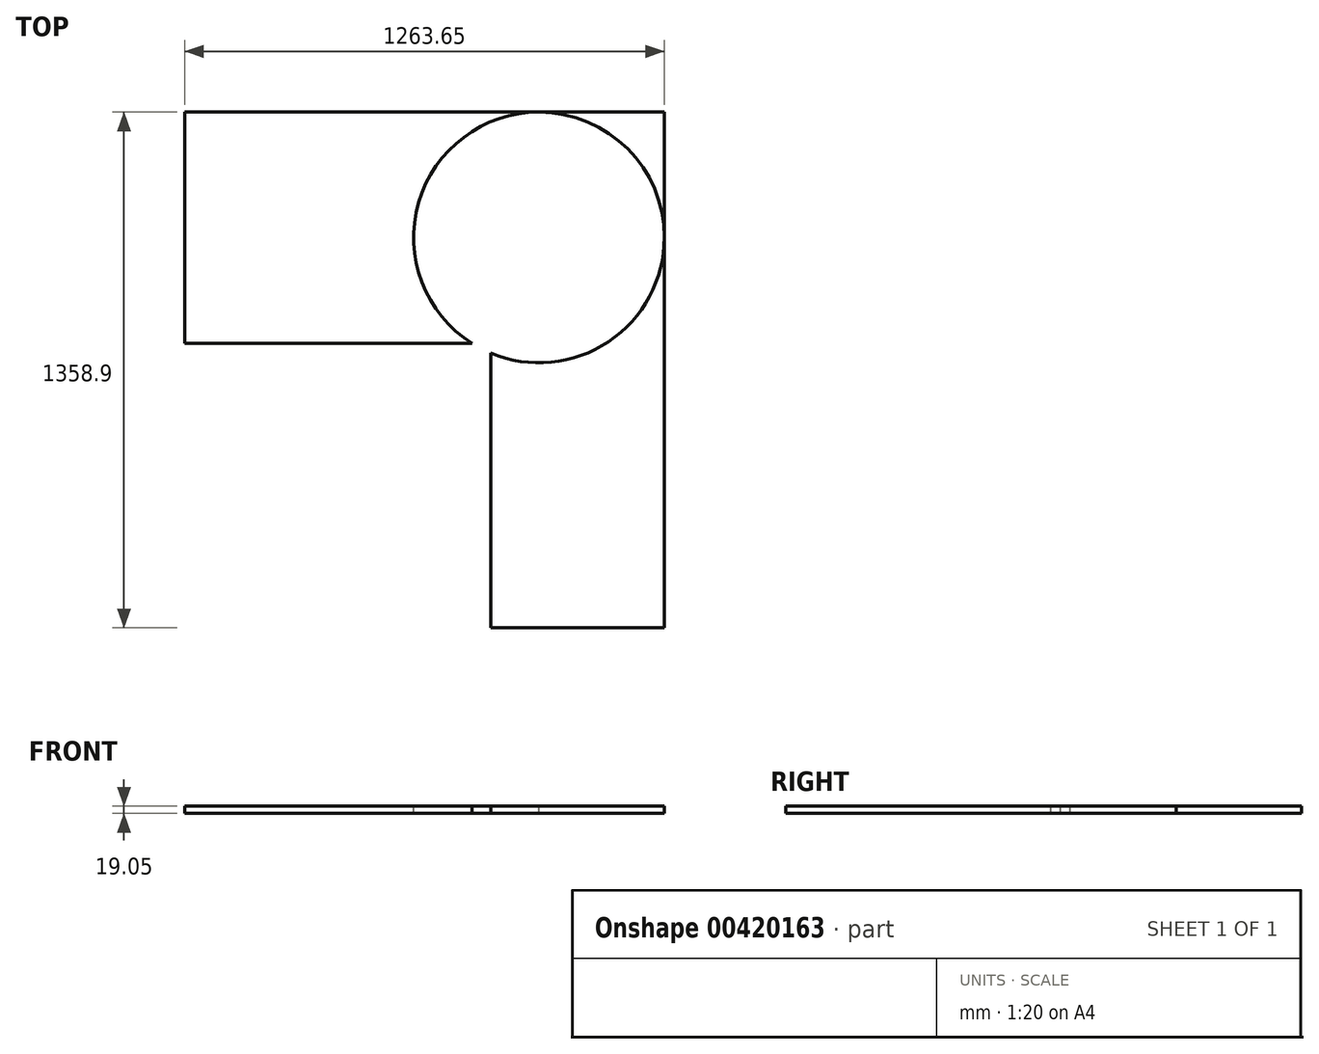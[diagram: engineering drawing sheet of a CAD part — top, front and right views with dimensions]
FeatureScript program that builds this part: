
annotation { "Feature Type Name" : "Feature", "Feature Type Description" : "" }
export const myFeature = defineFeature(function(context is Context, id is Id, definition is map)
    precondition{}
    {
        {
            var Q0;
            Q0=qCreatedBy(makeId("Top.planeOp"),FACE);
            var sketch = newSketch(context, id + "F0", { "sketchPlane" : qUnion([Q0])});
            skLineSegment(sketch, "E0", {"start": v(0, 0) * mm, "end": v(-1263.65, 0) * mm});
            skLineSegment(sketch, "E1", {"start": v(-1263.65, 0) * mm, "end": v(-1263.65, -609.6) * mm});
            skLineSegment(sketch, "E2", {"start": v(-457.2, -1358.9) * mm, "end": v(0, -1358.9) * mm});
            skLineSegment(sketch, "E3", {"start": v(0, -1358.9) * mm, "end": v(0, 0) * mm});
            skLineSegment(sketch, "E4", {"start": v(-1263.65, -609.6) * mm, "end": v(-457.2, -609.6) * mm});
            skLineSegment(sketch, "E5", {"start": v(-457.2, -609.6) * mm, "end": v(-457.2, -1358.9) * mm});
            skLineSegment(sketch, "E6.0", {"start": v(-1225.55, -38.1) * mm, "end": v(-1225.55, -609.6) * mm});
            skLineSegment(sketch, "E6.1", {"start": v(-38.1, -38.1) * mm, "end": v(-1225.55, -38.1) * mm});
            skLineSegment(sketch, "E6.2", {"start": v(-38.1, -1320.8) * mm, "end": v(-38.1, -38.1) * mm});
            skLineSegment(sketch, "E6.3", {"start": v(-457.2, -1320.8) * mm, "end": v(-38.1, -1320.8) * mm});
            skLineSegment(sketch, "E7", {"start": v(-1225.55, -609.6) * mm, "end": v(-1263.65, -609.6) * mm});
            skLineSegment(sketch, "E8", {"start": v(-457.2, -1320.8) * mm, "end": v(-457.2, -1358.9) * mm});
            skSolve(sketch);
        }
        {
            var Q0;
            Q0 = qSketchRegion(id + "F0", true);
            extrude(context, id + "F1", {"entities" : qUnion([Q0]), "depth" : 19.05 * mm});
        }
        {
            var Q0;
            Q0=makeQuery(id+"F1.opExtrude","CAP_FACE",FACE,{"disambiguationData":[OSD([sQuery(id+"F0.wireOp",EDGE,"E0"),sQuery(id+"F0.wireOp",EDGE,"E1"),sQuery(id+"F0.wireOp",EDGE,"E2"),sQuery(id+"F0.wireOp",EDGE,"E3"),sQuery(id+"F0.wireOp",EDGE,"E4"),sQuery(id+"F0.wireOp",EDGE,"E5"),sQuery(id+"F0.wireOp",EDGE,"E7"),sQuery(id+"F0.wireOp",EDGE,"E8")])],"isStart":false});
            var sketch = newSketch(context, id + "F2", { "sketchPlane" : qUnion([Q0])});
            skCircle(sketch, "E9", {"center": v(-330.2, -330.2) * mm, "radius": 330.2 * mm});
            skSolve(sketch);
        }
        {
            var Q0;
            {var subQ0=sQuery(id+"F2.wireOp",EDGE,"E9");var subQ7=makeQuery(id+"F2.imprint","INTERSECT",VERTEX,{"derivedFrom":[makeQuery(id+"F1.opExtrude","CAP_EDGE",EDGE,{"disambiguationData":[OSD([sQuery(id+"F0.wireOp",EDGE,"E0")])],"isStart":false}),subQ0]});Q0=makeQuery(id+"F2.imprint","IMPRINT",FACE,{"disambiguationData":[TD([[makeQuery(id+"F2.imprint","IMPRINT",EDGE,{"disambiguationData":[TD([[subQ7,1.0]])],"derivedFrom":subQ0}),1.0]])]});}
            extrude(context, id + "F3", {"entities" : qUnion([Q0]), "operationType" : NewBodyOperationType.REMOVE, "oppositeDirection" : true, "depth" : 25.4 * mm});
        }
    });
